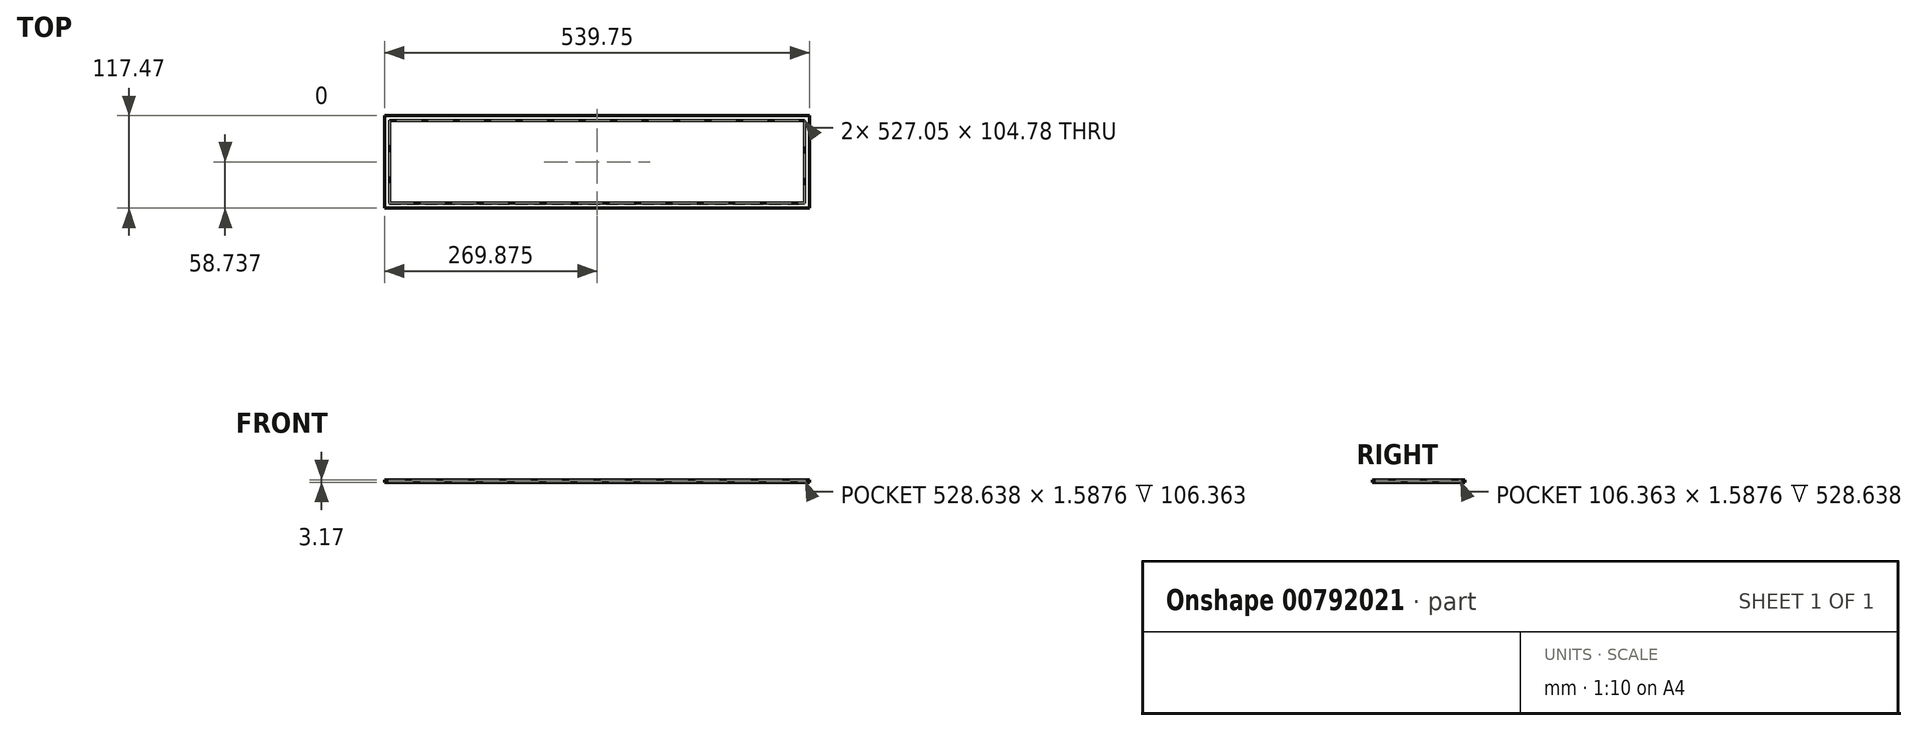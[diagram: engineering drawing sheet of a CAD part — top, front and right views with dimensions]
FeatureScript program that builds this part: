
annotation { "Feature Type Name" : "Feature", "Feature Type Description" : "" }
export const myFeature = defineFeature(function(context is Context, id is Id, definition is map)
    precondition{}
    {
        {
            var Q0;
            Q0=qCreatedBy(makeId("Top.planeOp"),FACE);
            var sketch = newSketch(context, id + "F0", { "sketchPlane" : qUnion([Q0])});
            skLineSegment(sketch, "E0", {"start": v(0, 0) * mm, "end": v(0, 117.48) * mm});
            skLineSegment(sketch, "E1", {"start": v(0, 117.48) * mm, "end": v(539.75, 117.48) * mm});
            skLineSegment(sketch, "E2", {"start": v(539.75, 117.48) * mm, "end": v(539.75, 0) * mm});
            skLineSegment(sketch, "E3", {"start": v(539.75, 0) * mm, "end": v(0, 0) * mm});
            skLineSegment(sketch, "E4", {"start": v(6.35, 57.15) * mm, "end": v(6.35, 111.13) * mm});
            skLineSegment(sketch, "E5", {"start": v(6.35, 111.13) * mm, "end": v(533.4, 111.13) * mm});
            skLineSegment(sketch, "E6", {"start": v(533.4, 111.13) * mm, "end": v(533.4, 6.35) * mm});
            skLineSegment(sketch, "E7", {"start": v(533.4, 6.35) * mm, "end": v(6.35, 6.35) * mm});
            skLineSegment(sketch, "E8", {"start": v(6.35, 6.35) * mm, "end": v(6.35, 57.15) * mm});
            skSolve(sketch);
        }
        {
            var Q0;
            Q0=makeQuery(id+"F0.imprint","IMPRINT",FACE,{"disambiguationData":[TD([[makeQuery(id+"F0.imprint","IMPRINT",EDGE,{"derivedFrom":sQuery(id+"F0.wireOp",EDGE,"E0")}),-1.0]])]});
            extrude(context, id + "F1", {"entities" : qUnion([Q0]), "depth" : 3.17 * mm, "offsetDistance" : 25.4 * mm});
        }
        {
            var Q0;
            Q0=qCreatedBy(makeId("Top.planeOp"),FACE);
            var sketch = newSketch(context, id + "F2", { "sketchPlane" : qUnion([Q0])});
            skLineSegment(sketch, "E9", {"start": v(0, 0) * mm, "end": v(6.35, 0) * mm});
            skLineSegment(sketch, "E10", {"start": v(6.35, 0) * mm, "end": v(6.35, 6.35) * mm});
            skLineSegment(sketch, "E11.bottom", {"start": v(6.35, 6.35) * mm, "end": v(534.99, 6.35) * mm});
            skLineSegment(sketch, "E11.top", {"start": v(6.35, 112.71) * mm, "end": v(534.99, 112.71) * mm});
            skLineSegment(sketch, "E11.left", {"start": v(6.35, 6.35) * mm, "end": v(6.35, 112.71) * mm});
            skLineSegment(sketch, "E11.right", {"start": v(534.99, 6.35) * mm, "end": v(534.99, 112.71) * mm});
            skSolve(sketch);
        }
        {
            var Q0;
            Q0=makeQuery(id+"F2.imprint","IMPRINT",FACE,{"disambiguationData":[TD([[makeQuery(id+"F2.imprint","IMPRINT",EDGE,{"derivedFrom":sQuery(id+"F2.wireOp",EDGE,"E11.bottom")}),1.0]])]});
            extrude(context, id + "F3", {"entities" : qUnion([Q0]), "depth" : 1.59 * mm, "offsetDistance" : 25.4 * mm});
        }
        {
            var Q0;
            Q0=makeQuery(id+"F3.opExtrude","SWEPT_BODY",BODY,{"disambiguationData":[OSD([sQuery(id+"F2.wireOp",EDGE,"E11.bottom"),sQuery(id+"F2.wireOp",EDGE,"E11.top"),sQuery(id+"F2.wireOp",EDGE,"E11.left"),sQuery(id+"F2.wireOp",EDGE,"E11.right")])]});
            transform(context, id + "F4", {"entities" : qUnion([Q0]), "transformType" : TransformType.TRANSLATION_3D, "dx" : -0.8 * mm, "dy" : -0.8 * mm, "dz" : 0.8 * mm, "makeCopy" : false});
        }
        {
            var Q0;
            Q0=makeQuery(id+"F3.opExtrude","CAP_FACE",FACE,{"disambiguationData":[OSD([sQuery(id+"F2.wireOp",EDGE,"E11.bottom"),sQuery(id+"F2.wireOp",EDGE,"E11.top"),sQuery(id+"F2.wireOp",EDGE,"E11.left"),sQuery(id+"F2.wireOp",EDGE,"E11.right")])],"isStart":false});
            extrude(context, id + "F5", {"entities" : qUnion([Q0]), "operationType" : NewBodyOperationType.REMOVE, "oppositeDirection" : true, "depth" : 1.59 * mm, "offsetDistance" : 25.4 * mm});
        }
    });
